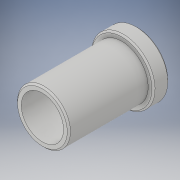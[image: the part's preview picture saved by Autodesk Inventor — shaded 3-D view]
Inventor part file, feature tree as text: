
AUTODESK INVENTOR PART (.ipt)
format: ipt  version: 2018 (Build 220112000, 112)  size: 125,440 bytes
history: native  units: mm
features: revolve x1, chamfer x1, sketch x1
ambient origin geometry x8: Origin, YZ Plane, XZ Plane, XY Plane, X Axis, Y Axis, Z Axis, Center Point
bodies: Solid1 (feature_tree)
feature tree (3):
  revolve  "Revolution1"  [1 undecoded]
  chamfer  "Chamfer1"  Distance=2.5mm
  sketch  "Sketch1"  dims[d0=9.0mm d1=2.0mm d2=2.5mm d3=3.0mm d4=1.5mm d5=9.0mm d6=90.0deg d7=0.15mm d8=2.0mm d9=45.0deg]
note: 1 required parameter value undecoded (feature->parameter linkage not recoverable at this tier; creation-order binding heuristic only, values carry confidence <= 0.55)
